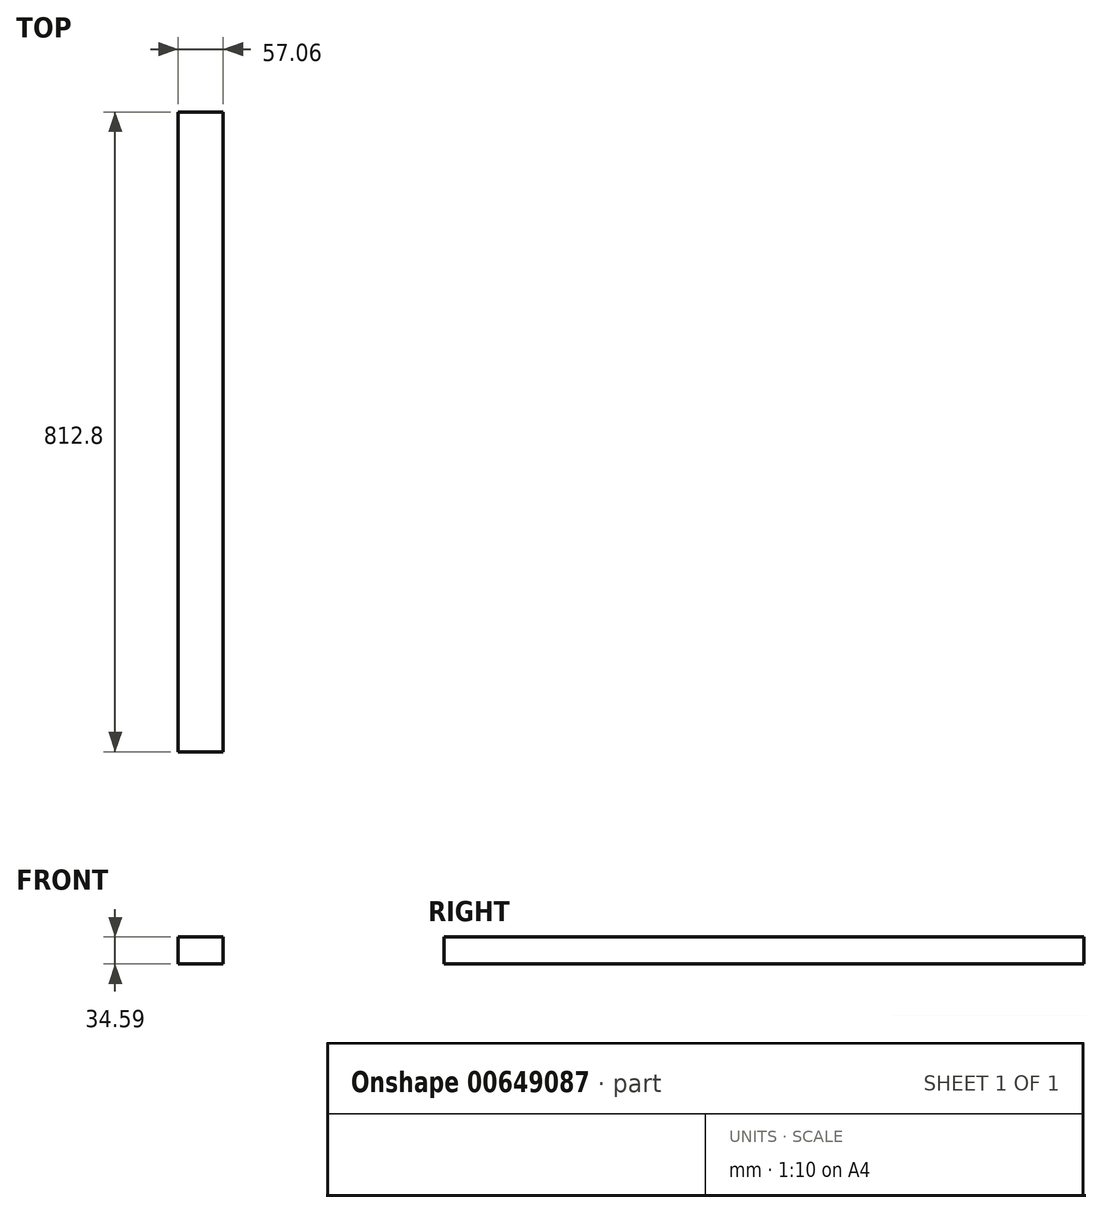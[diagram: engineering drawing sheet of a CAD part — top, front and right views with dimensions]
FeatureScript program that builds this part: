
annotation { "Feature Type Name" : "Feature", "Feature Type Description" : "" }
export const myFeature = defineFeature(function(context is Context, id is Id, definition is map)
    precondition{}
    {
        {
            var Q0;
            Q0=qCreatedBy(makeId("Front.planeOp"),FACE);
            var sketch = newSketch(context, id + "F0", { "sketchPlane" : qUnion([Q0])});
            skLineSegment(sketch, "E0.bottom", {"start": v(-46.5, 31.52) * mm, "end": v(10.55, 31.52) * mm});
            skLineSegment(sketch, "E0.top", {"start": v(-46.5, -3.07) * mm, "end": v(10.55, -3.07) * mm});
            skLineSegment(sketch, "E0.left", {"start": v(-46.5, 31.52) * mm, "end": v(-46.5, -3.07) * mm});
            skLineSegment(sketch, "E0.right", {"start": v(10.55, 31.52) * mm, "end": v(10.55, -3.07) * mm});
            skSolve(sketch);
        }
        {
            var Q0;
            Q0=makeQuery(id+"F0.imprint","IMPRINT",FACE,{"disambiguationData":[TD([[makeQuery(id+"F0.imprint","IMPRINT",EDGE,{"derivedFrom":sQuery(id+"F0.wireOp",EDGE,"E0.bottom")}),-1.0]])]});
            extrude(context, id + "F1", {"entities" : qUnion([Q0]), "depth" : 812.8 * mm, "offsetDistance" : 25.4 * mm});
        }
    });
